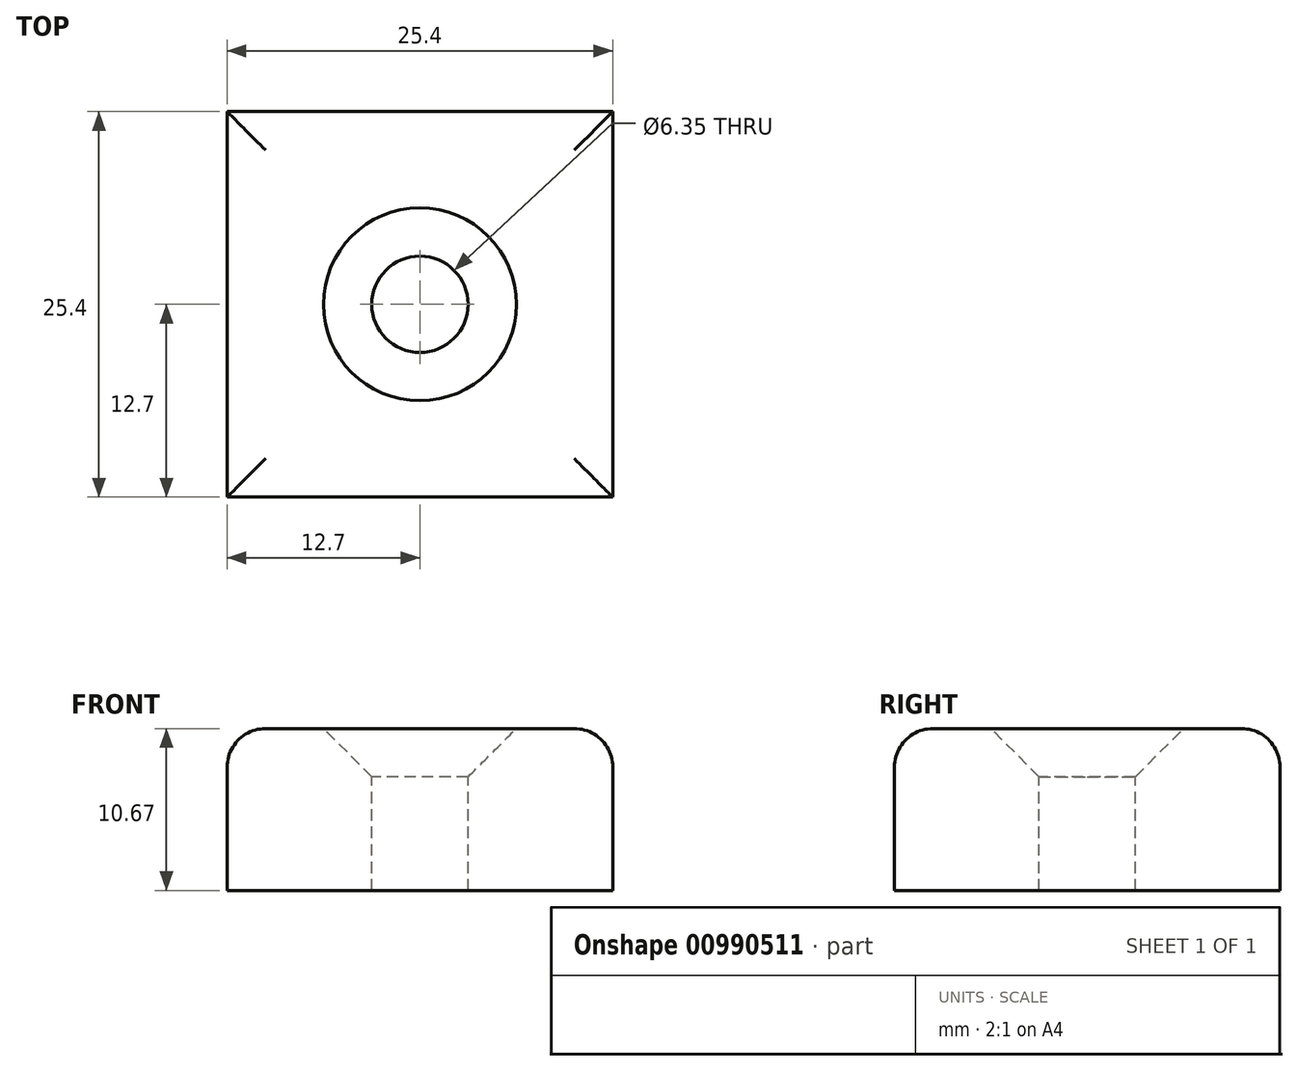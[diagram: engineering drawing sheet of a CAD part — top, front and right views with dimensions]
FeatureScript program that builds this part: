
annotation { "Feature Type Name" : "Feature", "Feature Type Description" : "" }
export const myFeature = defineFeature(function(context is Context, id is Id, definition is map)
    precondition{}
    {
        {
            var Q0;
            Q0=qCreatedBy(makeId("Top.planeOp"),FACE);
            var sketch = newSketch(context, id + "F0", { "sketchPlane" : qUnion([Q0])});
            skLineSegment(sketch, "E0.bottom", {"start": v(-12.7, 12.7) * mm, "end": v(12.7, 12.7) * mm});
            skLineSegment(sketch, "E0.top", {"start": v(-12.7, -12.7) * mm, "end": v(12.7, -12.7) * mm});
            skLineSegment(sketch, "E0.left", {"start": v(-12.7, 12.7) * mm, "end": v(-12.7, -12.7) * mm});
            skLineSegment(sketch, "E0.right", {"start": v(12.7, 12.7) * mm, "end": v(12.7, -12.7) * mm});
            skSolve(sketch);
        }
        {
            var Q0;
            Q0 = qSketchRegion(id + "F0", true);
            extrude(context, id + "F1", {"entities" : qUnion([Q0]), "depth" : 10.67 * mm, "offsetDistance" : 25.4 * mm});
        }
        {
            var Q0;
            Q0=makeQuery(id+"F1.opExtrude","CAP_EDGE",EDGE,{"disambiguationData":[OSD([sQuery(id+"F0.wireOp",EDGE,"E0.top")])],"isStart":false});
            var Q1;
            Q1=makeQuery(id+"F1.opExtrude","CAP_EDGE",EDGE,{"disambiguationData":[OSD([sQuery(id+"F0.wireOp",EDGE,"E0.bottom")])],"isStart":false});
            var Q2;
            Q2=makeQuery(id+"F1.opExtrude","CAP_EDGE",EDGE,{"disambiguationData":[OSD([sQuery(id+"F0.wireOp",EDGE,"E0.right")])],"isStart":false});
            var Q3;
            Q3=makeQuery(id+"F1.opExtrude","CAP_EDGE",EDGE,{"disambiguationData":[OSD([sQuery(id+"F0.wireOp",EDGE,"E0.left")])],"isStart":false});
            fillet(context, id + "F2", {"entities" : qUnion([Q0, Q1, Q2, Q3]), "radius" : 2.54 * mm, "tangentPropagation" : true, "allowEdgeOverflow" : false});
        }
        {
            var Q0;
            Q0=makeQuery(id+"F1.opExtrude","CAP_FACE",FACE,{"disambiguationData":[OSD([sQuery(id+"F0.wireOp",EDGE,"E0.bottom"),sQuery(id+"F0.wireOp",EDGE,"E0.top"),sQuery(id+"F0.wireOp",EDGE,"E0.left"),sQuery(id+"F0.wireOp",EDGE,"E0.right")])],"isStart":false});
            var sketch = newSketch(context, id + "F3", { "sketchPlane" : qUnion([Q0])});
            skPoint(sketch, "E1", {"position": v(0, 0) * mm});
            skSolve(sketch);
        }
        {
            var Q0;
            Q0=sQuery(id+"F3.wireOp",VERTEX,"E1");
            var Q1;
            Q1=makeQuery(id+"F1.opExtrude","SWEPT_BODY",BODY,{"disambiguationData":[OSD([sQuery(id+"F0.wireOp",EDGE,"E0.bottom"),sQuery(id+"F0.wireOp",EDGE,"E0.top"),sQuery(id+"F0.wireOp",EDGE,"E0.left"),sQuery(id+"F0.wireOp",EDGE,"E0.right")])]});
            hole(context, id + "F4", {"style" : HoleStyle.C_SINK, "endStyle" : HoleEndStyle.THROUGH, "holeDiameter" : 6.35 * mm, "cSinkDiameter" : 12.7 * mm, "cSinkAngle" : 90 * degree, "majorDiameter" : 6.35 * mm, "isTappedThrough" : true, "tappedDepth" : 12.7 * mm, "tapClearance" : 3, "locations" : qUnion([Q0]), "scope" : qUnion([Q1])});
        }
    });
